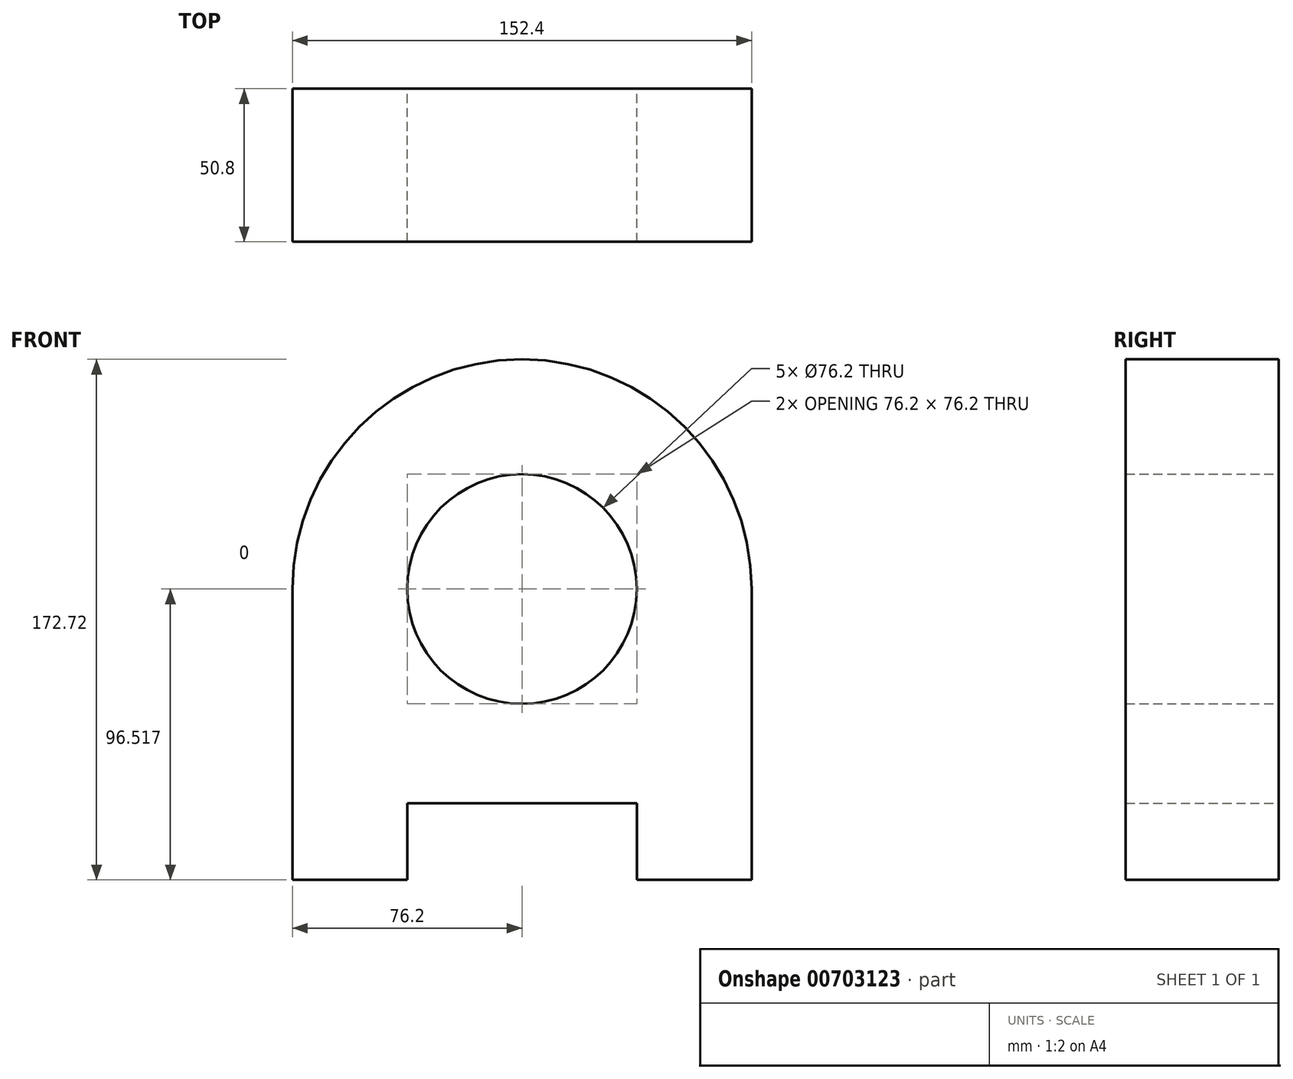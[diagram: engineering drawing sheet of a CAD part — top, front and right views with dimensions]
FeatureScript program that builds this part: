
annotation { "Feature Type Name" : "Feature", "Feature Type Description" : "" }
export const myFeature = defineFeature(function(context is Context, id is Id, definition is map)
    precondition{}
    {
        {
            var Q0;
            Q0=qCreatedBy(makeId("Front.planeOp"),FACE);
            var sketch = newSketch(context, id + "F0", { "sketchPlane" : qUnion([Q0])});
            skLineSegment(sketch, "E0.bottom", {"start": v(-77.52, 27.59) * mm, "end": v(74.88, 27.59) * mm});
            skLineSegment(sketch, "E0.top", {"start": v(-77.52, -43.53) * mm, "end": v(74.88, -43.53) * mm});
            skLineSegment(sketch, "E0.left", {"start": v(-77.52, 27.59) * mm, "end": v(-77.52, -43.53) * mm});
            skLineSegment(sketch, "E0.right", {"start": v(74.88, 27.59) * mm, "end": v(74.88, -43.53) * mm});
            skArc(sketch, "E1", {"start": v(74.88, 27.59) * mm, "mid": v(-1.32, 103.79) * mm, "end": v(-77.52, 27.59) * mm});
            skLineSegment(sketch, "E2", {"start": v(0, 103.78) * mm, "end": v(-1.32, 27.59) * mm});
            skLineSegment(sketch, "E3.bottom", {"start": v(-77.52, -43.53) * mm, "end": v(-39.42, -43.53) * mm});
            skLineSegment(sketch, "E3.top", {"start": v(-77.52, -68.93) * mm, "end": v(-39.42, -68.93) * mm});
            skLineSegment(sketch, "E3.left", {"start": v(-77.52, -43.53) * mm, "end": v(-77.52, -68.93) * mm});
            skLineSegment(sketch, "E3.right", {"start": v(-39.42, -43.53) * mm, "end": v(-39.42, -68.93) * mm});
            skLineSegment(sketch, "E4.bottom", {"start": v(74.88, -43.53) * mm, "end": v(36.78, -43.53) * mm});
            skLineSegment(sketch, "E4.top", {"start": v(74.88, -68.93) * mm, "end": v(36.78, -68.93) * mm});
            skLineSegment(sketch, "E4.left", {"start": v(74.88, -43.53) * mm, "end": v(74.88, -68.93) * mm});
            skLineSegment(sketch, "E4.right", {"start": v(36.78, -43.53) * mm, "end": v(36.78, -68.93) * mm});
            skSolve(sketch);
        }
        {
            var Q0;
            Q0 = qSketchRegion(id + "F0", true);
            extrude(context, id + "F1", {"entities" : qUnion([Q0]), "depth" : 50.8 * mm, "offsetDistance" : 25.4 * mm});
        }
        {
            var Q0;
            Q0=sQuery(id+"F0.wireOp",VERTEX,"E2.end");
            var Q1;
            Q1=makeQuery(id+"F1.opExtrude","SWEPT_BODY",BODY,{"disambiguationData":[OSD([sQuery(id+"F0.wireOp",EDGE,"E0.top"),sQuery(id+"F0.wireOp",EDGE,"E0.left"),sQuery(id+"F0.wireOp",EDGE,"E0.right"),sQuery(id+"F0.wireOp",EDGE,"E1"),sQuery(id+"F0.wireOp",EDGE,"E3.top"),sQuery(id+"F0.wireOp",EDGE,"E3.left"),sQuery(id+"F0.wireOp",EDGE,"E3.right"),sQuery(id+"F0.wireOp",EDGE,"E4.top"),sQuery(id+"F0.wireOp",EDGE,"E4.left"),sQuery(id+"F0.wireOp",EDGE,"E4.right")])]});
            hole(context, id + "F2", {"style" : HoleStyle.SIMPLE, "endStyle" : HoleEndStyle.THROUGH, "oppositeDirection" : true, "holeDiameter" : 76.2 * mm, "majorDiameter" : 6.35 * mm, "isTappedThrough" : true, "tappedDepth" : 12.7 * mm, "tapClearance" : 3, "locations" : qUnion([Q0]), "scope" : qUnion([Q1])});
        }
    });
